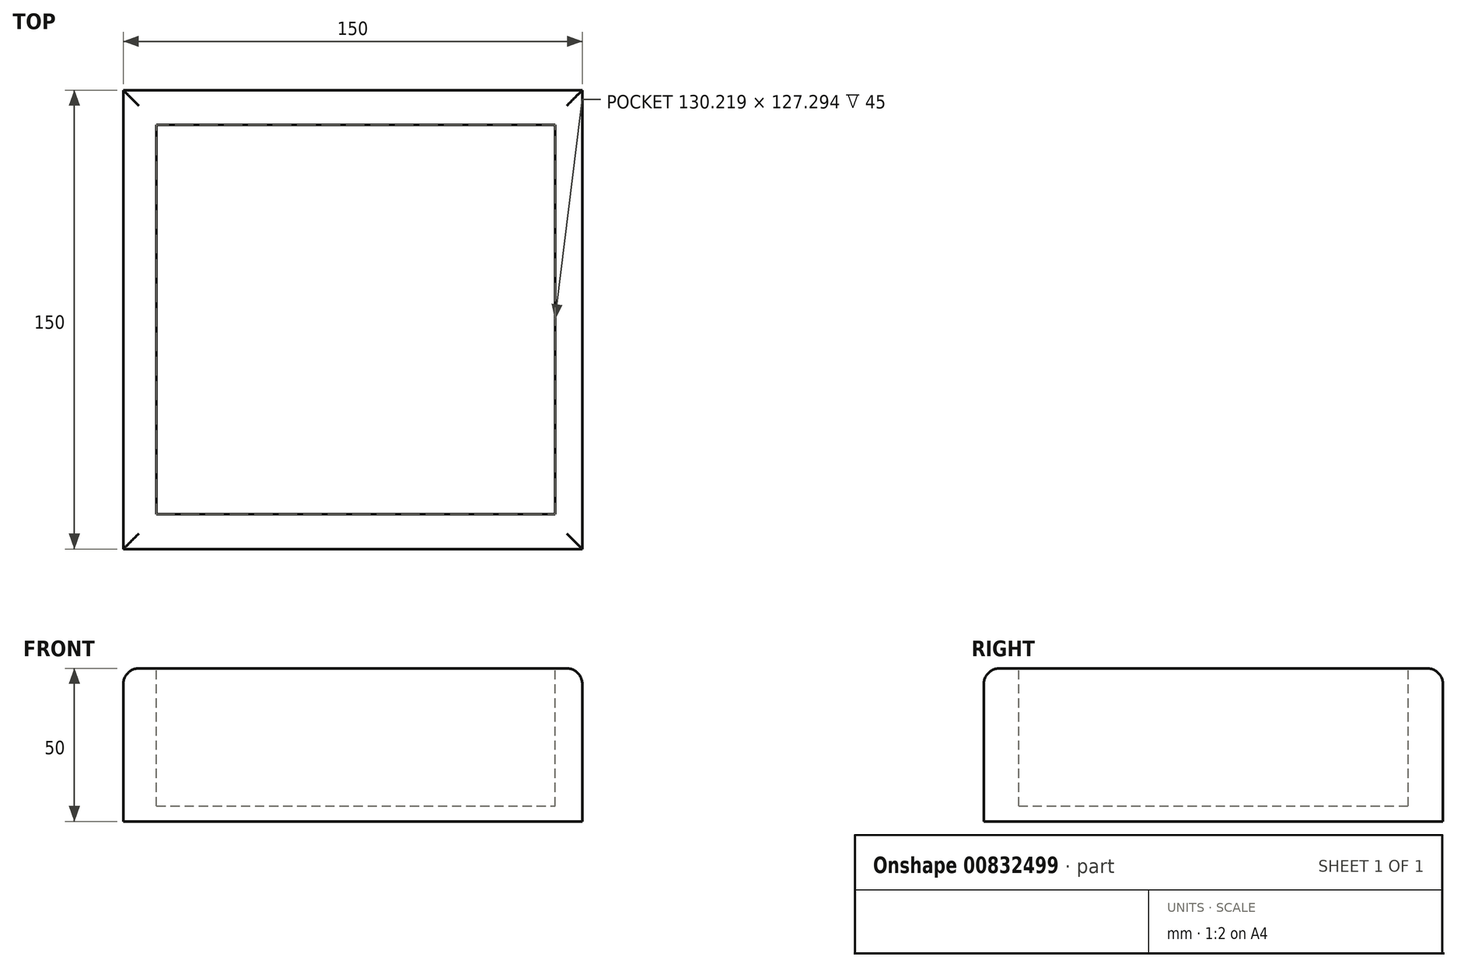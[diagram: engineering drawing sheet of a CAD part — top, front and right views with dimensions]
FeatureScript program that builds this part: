
annotation { "Feature Type Name" : "Feature", "Feature Type Description" : "" }
export const myFeature = defineFeature(function(context is Context, id is Id, definition is map)
    precondition{}
    {
        {
            var Q0;
            Q0=qCreatedBy(makeId("Top.planeOp"),FACE);
            var sketch = newSketch(context, id + "F0", { "sketchPlane" : qUnion([Q0])});
            skLineSegment(sketch, "E0.bottom", {"start": v(75, -75) * mm, "end": v(-75, -75) * mm});
            skLineSegment(sketch, "E0.top", {"start": v(75, 75) * mm, "end": v(-75, 75) * mm});
            skLineSegment(sketch, "E0.left", {"start": v(75, -75) * mm, "end": v(75, 75) * mm});
            skLineSegment(sketch, "E0.right", {"start": v(-75, -75) * mm, "end": v(-75, 75) * mm});
            skPoint(sketch, "E0.middle", {"position": v(0, 0) * mm});
            skSolve(sketch);
        }
        {
            var Q0;
            Q0=makeQuery(id+"F0.imprint","IMPRINT",FACE,{"disambiguationData":[TD([[makeQuery(id+"F0.imprint","IMPRINT",EDGE,{"derivedFrom":sQuery(id+"F0.wireOp",EDGE,"E0.bottom")}),-1.0]])]});
            extrude(context, id + "F1", {"entities" : qUnion([Q0]), "depth" : 50 * mm, "offsetDistance" : 25.4 * mm});
        }
        {
            var Q0;
            Q0=makeQuery(id+"F1.opExtrude","CAP_FACE",FACE,{"disambiguationData":[OSD([sQuery(id+"F0.wireOp",EDGE,"E0.bottom"),sQuery(id+"F0.wireOp",EDGE,"E0.top"),sQuery(id+"F0.wireOp",EDGE,"E0.left"),sQuery(id+"F0.wireOp",EDGE,"E0.right")])],"isStart":false});
            var sketch = newSketch(context, id + "F2", { "sketchPlane" : qUnion([Q0])});
            skLineSegment(sketch, "E1.bottom", {"start": v(-64.15, -63.6) * mm, "end": v(66.07, -63.6) * mm});
            skLineSegment(sketch, "E1.top", {"start": v(-64.15, 63.7) * mm, "end": v(66.07, 63.7) * mm});
            skLineSegment(sketch, "E1.left", {"start": v(-64.15, -63.6) * mm, "end": v(-64.15, 63.7) * mm});
            skLineSegment(sketch, "E1.right", {"start": v(66.07, -63.6) * mm, "end": v(66.07, 63.7) * mm});
            skSolve(sketch);
        }
        {
            var Q0;
            Q0=makeQuery(id+"F2.imprint","IMPRINT",FACE,{"disambiguationData":[TD([[makeQuery(id+"F2.imprint","IMPRINT",EDGE,{"derivedFrom":sQuery(id+"F2.wireOp",EDGE,"E1.bottom")}),1.0]])]});
            extrude(context, id + "F3", {"entities" : qUnion([Q0]), "operationType" : NewBodyOperationType.REMOVE, "oppositeDirection" : true, "depth" : 45 * mm, "offsetDistance" : 25.4 * mm});
        }
        {
            var Q0;
            Q0=makeQuery(id+"F1.opExtrude","CAP_EDGE",EDGE,{"disambiguationData":[OSD([sQuery(id+"F0.wireOp",EDGE,"E0.top")])],"isStart":false});
            var Q1;
            Q1=makeQuery(id+"F1.opExtrude","CAP_EDGE",EDGE,{"disambiguationData":[OSD([sQuery(id+"F0.wireOp",EDGE,"E0.right")])],"isStart":false});
            var Q2;
            Q2=makeQuery(id+"F1.opExtrude","CAP_EDGE",EDGE,{"disambiguationData":[OSD([sQuery(id+"F0.wireOp",EDGE,"E0.bottom")])],"isStart":false});
            var Q3;
            Q3=makeQuery(id+"F1.opExtrude","CAP_EDGE",EDGE,{"disambiguationData":[OSD([sQuery(id+"F0.wireOp",EDGE,"E0.left")])],"isStart":false});
            var Q4;
            Q4=makeQuery(id+"F3.boolean.opBoolean","COPY",EDGE,{"derivedFrom":makeQuery(id+"F3.opExtrude","CAP_EDGE",EDGE,{"disambiguationData":[OSD([sQuery(id+"F2.wireOp",EDGE,"E1.right")])],"isStart":true})});
            var Q5;
            Q5=makeQuery(id+"F3.boolean.opBoolean","COPY",EDGE,{"derivedFrom":makeQuery(id+"F3.opExtrude","CAP_EDGE",EDGE,{"disambiguationData":[OSD([sQuery(id+"F2.wireOp",EDGE,"E1.bottom")])],"isStart":true})});
            var Q6;
            Q6=makeQuery(id+"F3.boolean.opBoolean","COPY",EDGE,{"derivedFrom":makeQuery(id+"F3.opExtrude","CAP_EDGE",EDGE,{"disambiguationData":[OSD([sQuery(id+"F2.wireOp",EDGE,"E1.left")])],"isStart":true})});
            var Q7;
            Q7=makeQuery(id+"F3.boolean.opBoolean","COPY",EDGE,{"derivedFrom":makeQuery(id+"F3.opExtrude","CAP_EDGE",EDGE,{"disambiguationData":[OSD([sQuery(id+"F2.wireOp",EDGE,"E1.top")])],"isStart":true})});
            fillet(context, id + "F4", {"entities" : qUnion([Q0, Q1, Q2, Q3, Q4, Q5, Q6, Q7]), "radius" : 5.08 * mm, "tangentPropagation" : true, "allowEdgeOverflow" : false});
        }
    });
